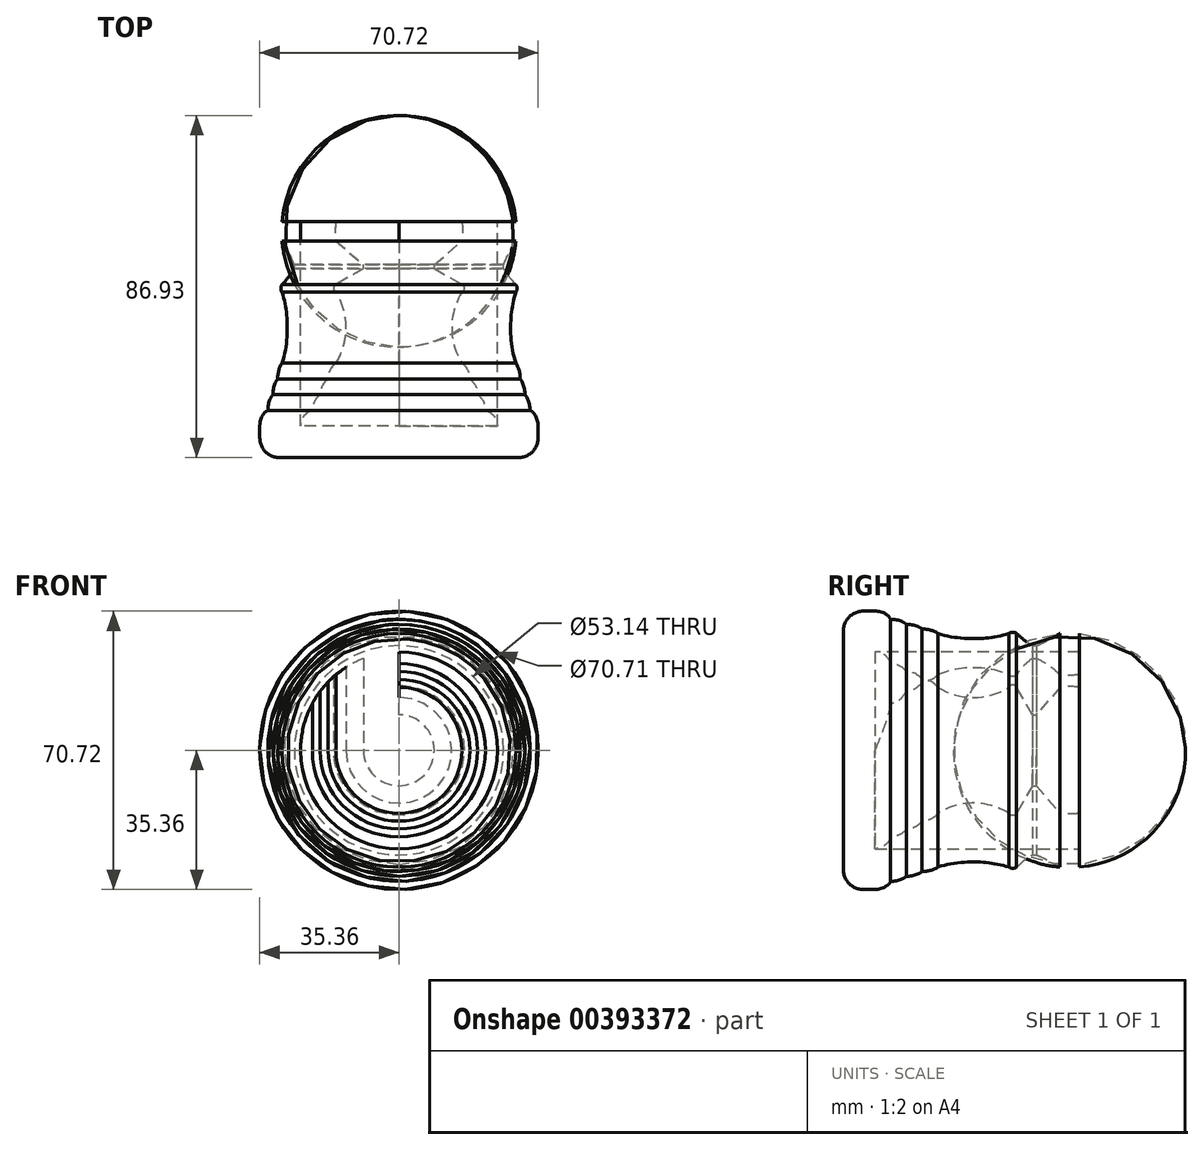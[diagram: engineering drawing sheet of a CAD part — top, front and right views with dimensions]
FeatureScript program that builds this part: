
annotation { "Feature Type Name" : "Feature", "Feature Type Description" : "" }
export const myFeature = defineFeature(function(context is Context, id is Id, definition is map)
    precondition{}
    {
        {
            var Q0;
            Q0=qCreatedBy(makeId("Top.planeOp"),FACE);
            var sketch = newSketch(context, id + "F0", { "sketchPlane" : qUnion([Q0])});
            skLineSegment(sketch, "E0", {"start": v(0, 79.26) * mm, "end": v(0, -96.88) * mm, "construction": true});
            skLineSegment(sketch, "E1", {"start": v(0, -49.67) * mm, "end": v(-25, -49.67) * mm});
            skLineSegment(sketch, "E2", {"start": v(-25, -49.67) * mm, "end": v(-25, -41.67) * mm});
            skLineSegment(sketch, "E3", {"start": v(-25, -41.67) * mm, "end": v(0, -41.67) * mm});
            skLineSegment(sketch, "E4", {"start": v(0, -41.67) * mm, "end": v(0, -37.67) * mm});
            skLineSegment(sketch, "E5", {"start": v(0, -37.67) * mm, "end": v(-22, -37.67) * mm});
            skLineSegment(sketch, "E6", {"start": v(-22, -37.67) * mm, "end": v(-22, -41.67) * mm});
            skLineSegment(sketch, "E7", {"start": v(0, -41.67) * mm, "end": v(0, -49.67) * mm});
            skLineSegment(sketch, "E8", {"start": v(123.46, 27.58) * mm, "end": v(126.72, 27.58) * mm});
            skLineSegment(sketch, "E9", {"start": v(126.72, 19.07) * mm, "end": v(126.72, 27.58) * mm});
            skLineSegment(sketch, "E10", {"start": v(0, -37.67) * mm, "end": v(0, -33.67) * mm});
            skLineSegment(sketch, "E11", {"start": v(0, -33.67) * mm, "end": v(-20, -33.67) * mm});
            skLineSegment(sketch, "E12", {"start": v(-20, -33.67) * mm, "end": v(-20, -37.67) * mm});
            skLineSegment(sketch, "E13", {"start": v(0, -33.67) * mm, "end": v(0, -29.67) * mm});
            skLineSegment(sketch, "E14", {"start": v(0, -29.67) * mm, "end": v(-1.47, -29.67) * mm});
            skLineSegment(sketch, "E15", {"start": v(-1.47, -29.67) * mm, "end": v(0, -29.67) * mm});
            skLineSegment(sketch, "E16", {"start": v(0, -29.67) * mm, "end": v(-18, -29.67) * mm});
            skLineSegment(sketch, "E17", {"start": v(-18, -29.67) * mm, "end": v(-18, -33.67) * mm});
            skLineSegment(sketch, "E18", {"start": v(0, -29.67) * mm, "end": v(0, -25.67) * mm});
            skLineSegment(sketch, "E19", {"start": v(0, -25.67) * mm, "end": v(-16, -25.67) * mm});
            skLineSegment(sketch, "E20", {"start": v(-16, -25.67) * mm, "end": v(-16, -29.67) * mm});
            skLineSegment(sketch, "E21", {"start": v(0, -25.67) * mm, "end": v(0, -7.67) * mm});
            skLineSegment(sketch, "E22", {"start": v(0, -7.67) * mm, "end": v(-16, -7.67) * mm});
            skArc(sketch, "E23", {"start": v(-16, -25.67) * mm, "mid": v(-13.42, -16.67) * mm, "end": v(-16, -7.67) * mm});
            skLineSegment(sketch, "E24", {"start": v(0, -7.67) * mm, "end": v(0, -5.67) * mm});
            skLineSegment(sketch, "E25", {"start": v(0, -5.67) * mm, "end": v(-16, -5.67) * mm});
            skLineSegment(sketch, "E26", {"start": v(-16, -5.67) * mm, "end": v(-16, -7.67) * mm});
            skLineSegment(sketch, "E27", {"start": v(0, -5.67) * mm, "end": v(0, -1.67) * mm});
            skLineSegment(sketch, "E28", {"start": v(0, -1.67) * mm, "end": v(-9, -1.67) * mm});
            skLineSegment(sketch, "E29", {"start": v(-9, -1.67) * mm, "end": v(-16, -5.67) * mm});
            skLineSegment(sketch, "E30", {"start": v(0, -1.67) * mm, "end": v(0, 0) * mm});
            skLineSegment(sketch, "E31", {"start": v(0, -1.67) * mm, "end": v(0, -0.67) * mm});
            skLineSegment(sketch, "E32", {"start": v(0, -0.67) * mm, "end": v(-9, -0.67) * mm});
            skLineSegment(sketch, "E33", {"start": v(-9, -0.67) * mm, "end": v(-9, -1.67) * mm});
            skLineSegment(sketch, "E34", {"start": v(0, -0.67) * mm, "end": v(0, 5.33) * mm});
            skLineSegment(sketch, "E35", {"start": v(0, 5.33) * mm, "end": v(-16, 5.33) * mm});
            skLineSegment(sketch, "E36", {"start": v(-16, 5.33) * mm, "end": v(-9, -0.67) * mm});
            skLineSegment(sketch, "E37", {"start": v(0, 5.33) * mm, "end": v(0, 10.33) * mm});
            skLineSegment(sketch, "E38", {"start": v(0, 10.33) * mm, "end": v(-16, 10.33) * mm});
            skLineSegment(sketch, "E39", {"start": v(-16, 10.33) * mm, "end": v(-16, 5.33) * mm});
            skArc(sketch, "E40", {"start": v(-22, -37.67) * mm, "mid": v(-24.17, -39.17) * mm, "end": v(-25, -41.67) * mm});
            skArc(sketch, "E41", {"start": v(-20, -33.67) * mm, "mid": v(-21.47, -35.43) * mm, "end": v(-22, -37.67) * mm});
            skArc(sketch, "E42", {"start": v(-18, -29.67) * mm, "mid": v(-19.47, -31.43) * mm, "end": v(-20, -33.67) * mm});
            skArc(sketch, "E43", {"start": v(-16, -25.67) * mm, "mid": v(-17.47, -27.43) * mm, "end": v(-18, -29.67) * mm});
            skArc(sketch, "E44", {"start": v(-16, -5.67) * mm, "mid": v(-16.58, -6.67) * mm, "end": v(-16, -7.67) * mm});
            skArc(sketch, "E45", {"start": v(-16, 10.33) * mm, "mid": v(-16.2, 7.83) * mm, "end": v(-16, 5.33) * mm});
            skArc(sketch, "E46", {"start": v(-9, -1.67) * mm, "mid": v(-8.77, -1.17) * mm, "end": v(-9, -0.67) * mm});
            skSolve(sketch);
        }
        {
            var Q0;
            Q0 = qSketchRegion(id + "F0", true);
            extrude(context, id + "F1", {"entities" : qUnion([Q0]), "depth" : 25 * mm});
        }
        {
            var Q0;
            Q0 = qSketchRegion(id + "F0", true);
            var Q1;
            Q1=makeQuery(id+"F1.opExtrude","CAP_FACE",FACE,{"disambiguationData":[OSD([sQuery(id+"F0.wireOp",EDGE,"E1"),sQuery(id+"F0.wireOp",EDGE,"E2"),sQuery(id+"F0.wireOp",EDGE,"E4"),sQuery(id+"F0.wireOp",EDGE,"E7"),sQuery(id+"F0.wireOp",EDGE,"E10"),sQuery(id+"F0.wireOp",EDGE,"E13"),sQuery(id+"F0.wireOp",EDGE,"E18"),sQuery(id+"F0.wireOp",EDGE,"E21"),sQuery(id+"F0.wireOp",EDGE,"E23"),sQuery(id+"F0.wireOp",EDGE,"E24"),sQuery(id+"F0.wireOp",EDGE,"E27"),sQuery(id+"F0.wireOp",EDGE,"E29"),sQuery(id+"F0.wireOp",EDGE,"E31"),sQuery(id+"F0.wireOp",EDGE,"E33"),sQuery(id+"F0.wireOp",EDGE,"E34"),sQuery(id+"F0.wireOp",EDGE,"E36"),sQuery(id+"F0.wireOp",EDGE,"E37"),sQuery(id+"F0.wireOp",EDGE,"E38"),sQuery(id+"F0.wireOp",EDGE,"E40"),sQuery(id+"F0.wireOp",EDGE,"E41"),sQuery(id+"F0.wireOp",EDGE,"E42"),sQuery(id+"F0.wireOp",EDGE,"E43"),sQuery(id+"F0.wireOp",EDGE,"E44"),sQuery(id+"F0.wireOp",EDGE,"E45")])],"isStart":false});
            var Q2;
            Q2=makeQuery(id+"F1.opExtrude","CAP_EDGE",EDGE,{"disambiguationData":[OSD([sQuery(id+"F0.wireOp",EDGE,"E4"),sQuery(id+"F0.wireOp",EDGE,"E7"),sQuery(id+"F0.wireOp",EDGE,"E10"),sQuery(id+"F0.wireOp",EDGE,"E13"),sQuery(id+"F0.wireOp",EDGE,"E18"),sQuery(id+"F0.wireOp",EDGE,"E21"),sQuery(id+"F0.wireOp",EDGE,"E24"),sQuery(id+"F0.wireOp",EDGE,"E27"),sQuery(id+"F0.wireOp",EDGE,"E31"),sQuery(id+"F0.wireOp",EDGE,"E34"),sQuery(id+"F0.wireOp",EDGE,"E37")])],"isStart":true});
            revolve(context, id + "F2", {"operationType" : NewBodyOperationType.ADD, "entities" : qUnion([Q0, Q1]), "axis" : qUnion([Q2]), "revolveType" : RevolveType.FULL});
        }
        {
            var Q0;
            {var subQ0=sQuery(id+"F0.wireOp",EDGE,"E2");var subQ1=sQuery(id+"F0.wireOp",EDGE,"E1");Q0=makeQuery(id+"F2.opRevolve","SWEPT_EDGE",EDGE,{"disambiguationData":[OSD([subQ1,subQ0]),TDD([makeQuery(id+"F1.opExtrude","CAP_VERTEX",VERTEX,{"disambiguationData":[OSD([subQ1,subQ0])],"isStart":false})])]});}
            fillet(context, id + "F3", {"entities" : qUnion([Q0]), "radius" : 5 * mm, "tangentPropagation" : true, "allowEdgeOverflow" : false});
        }
        {
            var Q0;
            {var subQ0=sQuery(id+"F0.wireOp",EDGE,"E1");Q0=makeQuery(id+"F2.boolean.opBoolean","MERGE",FACE,{"derivedFrom":[makeQuery(id+"F1.opExtrude","SWEPT_FACE",FACE,{"disambiguationData":[OSD([subQ0])]}),makeQuery(id+"F2.opRevolve","SWEPT_FACE",FACE,{"disambiguationData":[OSD([subQ0]),TDD([makeQuery(id+"F0.imprint","IMPRINT",EDGE,{"derivedFrom":subQ0})])]}),makeQuery(id+"F2.opRevolve","SWEPT_FACE",FACE,{"disambiguationData":[OSD([subQ0]),TDD([makeQuery(id+"F1.opExtrude","CAP_EDGE",EDGE,{"disambiguationData":[OSD([subQ0])],"isStart":false})])]})]});}
            var sketch = newSketch(context, id + "F4", { "sketchPlane" : qUnion([Q0])});
            skCircle(sketch, "E47", {"center": v(0, 0) * mm, "radius": 6 * mm});
            skSolve(sketch);
        }
        {
            var Q0;
            Q0=makeQuery(id+"F4.imprint","IMPRINT",FACE,{"disambiguationData":[TD([[makeQuery(id+"F4.imprint","IMPRINT",EDGE,{"derivedFrom":sQuery(id+"F4.wireOp",EDGE,"E47")}),1.0]])]});
            extrude(context, id + "F5", {"entities" : qUnion([Q0]), "operationType" : NewBodyOperationType.ADD, "oppositeDirection" : true, "depth" : 50 * mm});
        }
    });
